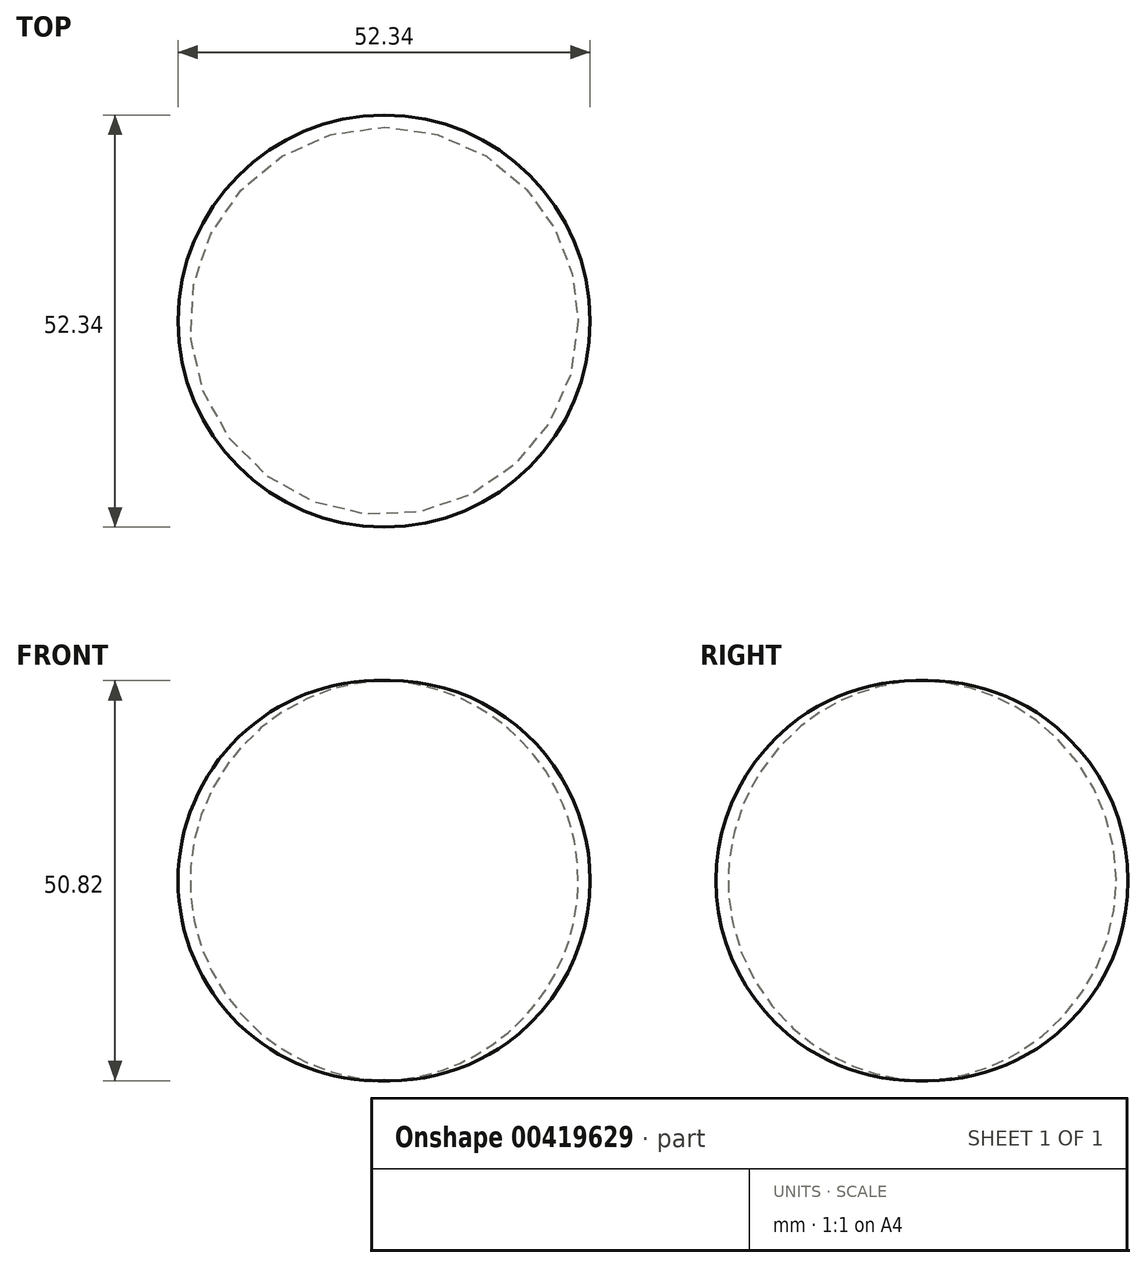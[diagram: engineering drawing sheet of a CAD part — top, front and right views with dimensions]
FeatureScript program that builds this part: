
annotation { "Feature Type Name" : "Feature", "Feature Type Description" : "" }
export const myFeature = defineFeature(function(context is Context, id is Id, definition is map)
    precondition{}
    {
        {
            var Q0;
            Q0=qCreatedBy(makeId("Front.planeOp"),FACE);
            var sketch = newSketch(context, id + "F0", { "sketchPlane" : qUnion([Q0])});
            skLineSegment(sketch, "E0", {"start": v(0, 0) * mm, "end": v(0, 50.8) * mm});
            skArc(sketch, "E1", {"start": v(0, 0) * mm, "mid": v(24.65, 25.4) * mm, "end": v(0, 50.8) * mm});
            skSolve(sketch);
        }
        {
            var Q0;
            Q0 = qSketchRegion(id + "F0", true);
            var Q1;
            Q1=sQuery(id+"F0.wireOp",EDGE,"E0");
            revolve(context, id + "F1", {"entities" : qUnion([Q0]), "axis" : qUnion([Q1]), "revolveType" : RevolveType.FULL});
        }
    });
